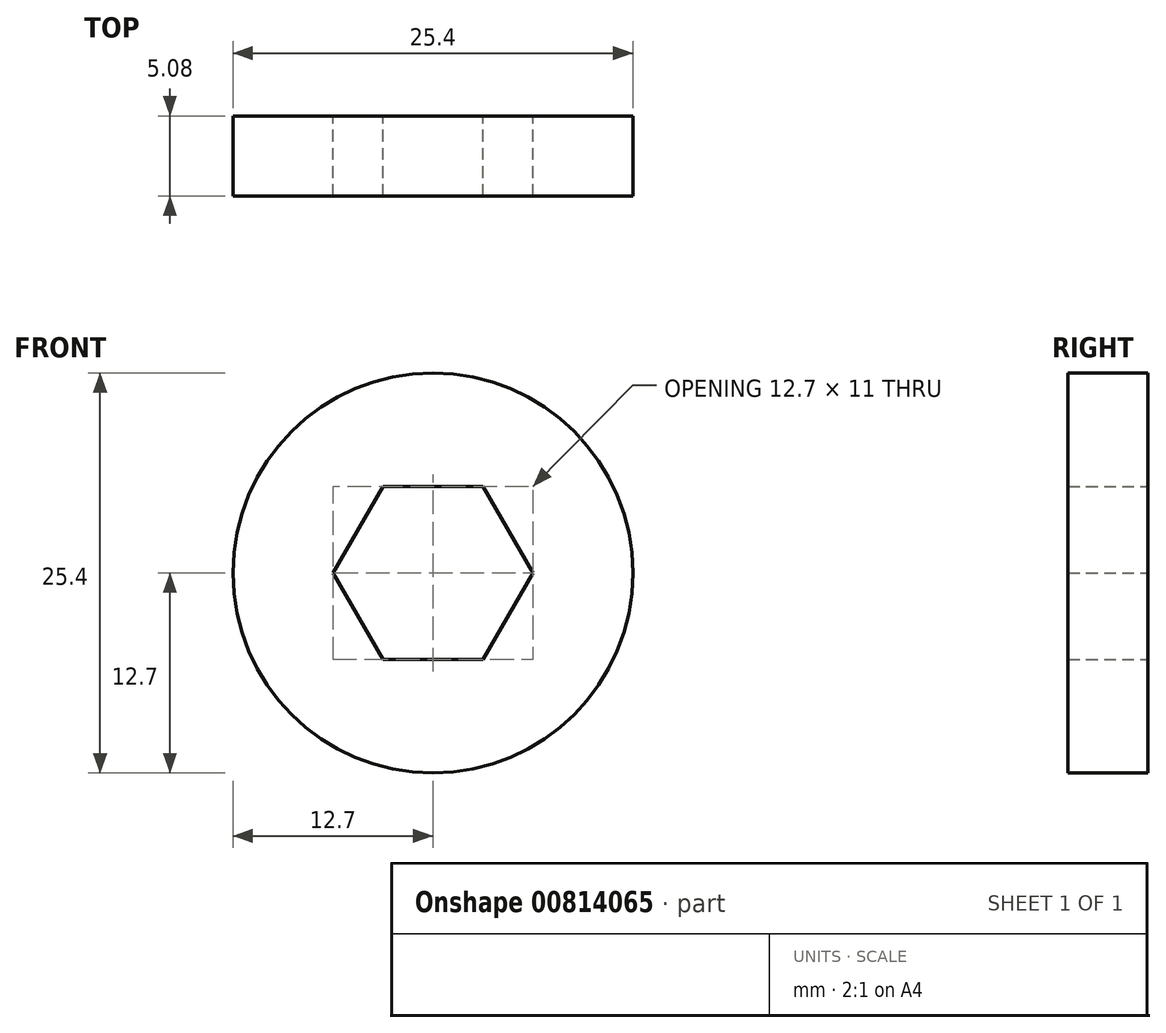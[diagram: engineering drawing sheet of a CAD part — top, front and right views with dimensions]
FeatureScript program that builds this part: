
annotation { "Feature Type Name" : "Feature", "Feature Type Description" : "" }
export const myFeature = defineFeature(function(context is Context, id is Id, definition is map)
    precondition{}
    {
        {
            var Q0;
            Q0=qCreatedBy(makeId("Front.planeOp"),FACE);
            var sketch = newSketch(context, id + "F0", { "sketchPlane" : qUnion([Q0])});
            skCircle(sketch, "E0", {"center": v(0, 0) * mm, "radius": 12.7 * mm});
            skCircle(sketch, "E1.cCircle", {"center": v(0, 0) * mm, "radius": 5.5 * mm, "construction": true});
            skLineSegment(sketch, "E1.0", {"start": v(-3.17, 5.5) * mm, "end": v(3.17, 5.5) * mm});
            skLineSegment(sketch, "E1.1", {"start": v(3.17, 5.5) * mm, "end": v(6.35, 0) * mm});
            skLineSegment(sketch, "E1.2", {"start": v(6.35, 0) * mm, "end": v(3.17, -5.5) * mm});
            skLineSegment(sketch, "E1.3", {"start": v(3.17, -5.5) * mm, "end": v(-3.17, -5.5) * mm});
            skLineSegment(sketch, "E1.4", {"start": v(-3.17, -5.5) * mm, "end": v(-6.35, 0) * mm});
            skLineSegment(sketch, "E1.5", {"start": v(-6.35, 0) * mm, "end": v(-3.17, 5.5) * mm});
            skPoint(sketch, "E1.0.midPoint", {"position": v(0, 5.5) * mm});
            skSolve(sketch);
        }
        {
            var Q0;
            Q0=makeQuery(id+"F0.imprint","IMPRINT",FACE,{"disambiguationData":[TD([[makeQuery(id+"F0.imprint","IMPRINT",EDGE,{"derivedFrom":sQuery(id+"F0.wireOp",EDGE,"E0")}),1.0]])]});
            extrude(context, id + "F1", {"entities" : qUnion([Q0]), "depth" : 5.08 * mm, "offsetDistance" : 25.4 * mm});
        }
    });
